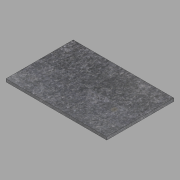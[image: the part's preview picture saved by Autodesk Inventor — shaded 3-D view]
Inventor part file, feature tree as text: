
AUTODESK INVENTOR PART (.ipt)
format: ipt  version: 2022.2 (Build 262287000, 287)  size: 106,496 bytes
history: native  units: in
note: dims shown in document units (in); Inventor stores cm internally (conversion verified against a paired STEP export)
features: extrude x1, sketch x1
ambient origin geometry x8: Origin, YZ Plane, XZ Plane, XY Plane, X Axis, Y Axis, Z Axis, Center Point
bodies: Solid1 (feature_tree)
feature tree (2):
  extrude  "Extrusion1"  Depth=24.0in
  sketch  "Sketch1"  dims[d0=36.0in d1=24.0in d2=1.0in d3=0.0in]
